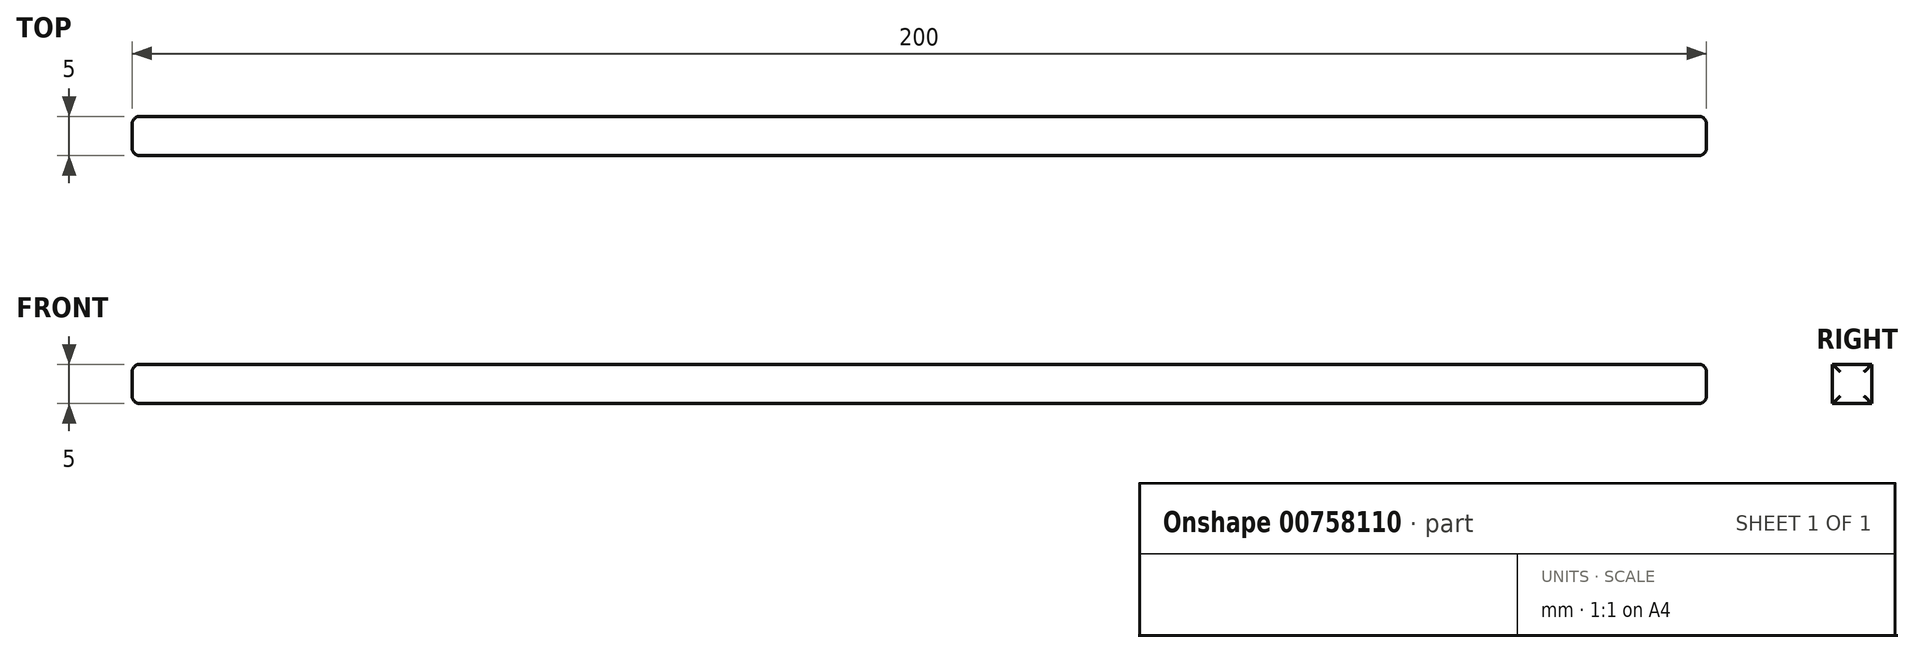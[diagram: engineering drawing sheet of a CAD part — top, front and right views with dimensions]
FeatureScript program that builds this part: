
annotation { "Feature Type Name" : "Feature", "Feature Type Description" : "" }
export const myFeature = defineFeature(function(context is Context, id is Id, definition is map)
    precondition{}
    {
        {
            var Q0;
            Q0=qCreatedBy(makeId("Top.planeOp"),FACE);
            var sketch = newSketch(context, id + "F0", { "sketchPlane" : qUnion([Q0])});
            skLineSegment(sketch, "E0.bottom", {"start": v(100, 2.5) * mm, "end": v(-100, 2.5) * mm});
            skLineSegment(sketch, "E0.top", {"start": v(100, -2.5) * mm, "end": v(-100, -2.5) * mm});
            skLineSegment(sketch, "E0.left", {"start": v(100, 2.5) * mm, "end": v(100, -2.5) * mm});
            skLineSegment(sketch, "E0.right", {"start": v(-100, 2.5) * mm, "end": v(-100, -2.5) * mm});
            skPoint(sketch, "E0.middle", {"position": v(0, 0) * mm});
            skSolve(sketch);
        }
        {
            var Q0;
            Q0 = qSketchRegion(id + "F0", true);
            extrude(context, id + "F1", {"entities" : qUnion([Q0]), "depth" : 5 * mm, "offsetDistance" : 25 * mm});
        }
        {
            var Q0;
            Q0=makeQuery(id+"F1.opExtrude","SWEPT_FACE",FACE,{"disambiguationData":[OSD([sQuery(id+"F0.wireOp",EDGE,"E0.right")])]});
            var Q1;
            Q1=makeQuery(id+"F1.opExtrude","SWEPT_FACE",FACE,{"disambiguationData":[OSD([sQuery(id+"F0.wireOp",EDGE,"E0.left")])]});
            fillet(context, id + "F2", {"entities" : qUnion([Q0, Q1]), "radius" : 1 * mm, "tangentPropagation" : true, "allowEdgeOverflow" : false});
        }
    });
